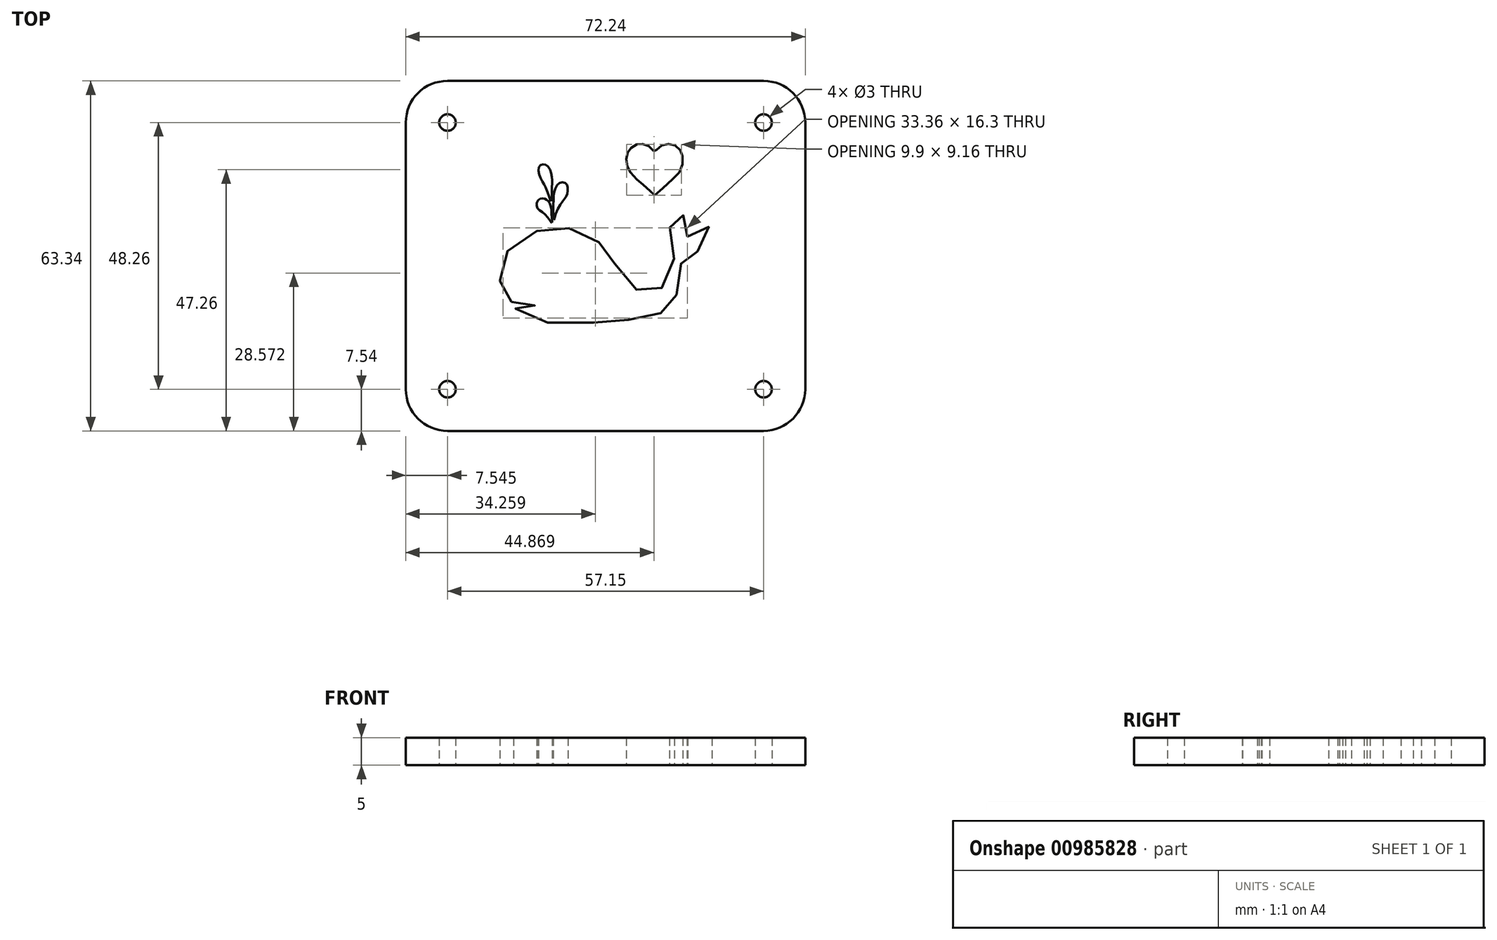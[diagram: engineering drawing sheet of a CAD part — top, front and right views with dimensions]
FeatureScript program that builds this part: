
annotation { "Feature Type Name" : "Feature", "Feature Type Description" : "" }
export const myFeature = defineFeature(function(context is Context, id is Id, definition is map)
    precondition{}
    {
        {
            var Q0;
            Q0=qCreatedBy(makeId("Top.planeOp"),FACE);
            var sketch = newSketch(context, id + "F0", { "sketchPlane" : qUnion([Q0])});
            skLineSegment(sketch, "E0.bottom", {"start": v(28.57, 31.67) * mm, "end": v(-28.58, 31.67) * mm});
            skLineSegment(sketch, "E0.top", {"start": v(28.58, -31.67) * mm, "end": v(-28.57, -31.67) * mm});
            skLineSegment(sketch, "E0.left", {"start": v(36.12, 24.13) * mm, "end": v(36.12, -24.13) * mm});
            skLineSegment(sketch, "E0.right", {"start": v(-36.12, 24.13) * mm, "end": v(-36.12, -24.13) * mm});
            skPoint(sketch, "E0.middle", {"position": v(0, 0) * mm});
            skPoint(sketch, "E1.visualSharp", {"position": v(-36.12, 31.67) * mm});
            skArc(sketch, "E1.filletArc", {"start": v(-28.58, 31.67) * mm, "mid": v(-33.9, 29.46) * mm, "end": v(-36.12, 24.13) * mm});
            skPoint(sketch, "E2.visualSharp", {"position": v(36.12, 31.67) * mm});
            skArc(sketch, "E2.filletArc", {"start": v(36.11, 24.13) * mm, "mid": v(33.9, 29.46) * mm, "end": v(28.57, 31.67) * mm});
            skPoint(sketch, "E3.visualSharp", {"position": v(36.12, -31.67) * mm});
            skArc(sketch, "E3.filletArc", {"start": v(28.58, -31.67) * mm, "mid": v(33.9, -29.46) * mm, "end": v(36.12, -24.13) * mm});
            skPoint(sketch, "E4.visualSharp", {"position": v(-36.11, -31.67) * mm});
            skArc(sketch, "E4.filletArc", {"start": v(-36.12, -24.13) * mm, "mid": v(-33.9, -29.46) * mm, "end": v(-28.57, -31.67) * mm});
            skCircle(sketch, "E5", {"center": v(-28.58, 24.13) * mm, "radius": 1.5 * mm});
            skCircle(sketch, "E6", {"center": v(28.57, 24.13) * mm, "radius": 1.5 * mm});
            skCircle(sketch, "E7", {"center": v(-28.57, -24.13) * mm, "radius": 1.5 * mm});
            skCircle(sketch, "E8", {"center": v(28.58, -24.13) * mm, "radius": 1.5 * mm});
            skFitSpline(sketch, "E9", {"points": [v(14.82, 3.5) * mm, v(16.2, 4.84) * mm, v(17.58, 5.43) * mm, v(18.71, 5.22) * mm, v(19.23, 4.15) * mm, v(18.37, 2.12) * mm, v(15.03, 0) * mm, v(14.37, -0.26) * mm, v(13.96, -0.4) * mm, v(13.7, -1.17) * mm, v(13.52, -1.93) * mm, v(13.25, -4.1) * mm, v(12.65, -7.62) * mm, v(12.02, -8.8) * mm, v(11.27, -9.7) * mm, v(9.38, -10.56) * mm, v(7.28, -10.99) * mm, v(3.97, -11.58) * mm, v(0.94, -12.03) * mm, v(-1.92, -12.1) * mm, v(-8.24, -12.13) * mm, v(-11.23, -11.95) * mm, v(-14.16, -11.03) * mm, v(-16.53, -9.26) * mm, v(-16.59, -9.08) * mm, v(-15.94, -9.26) * mm, v(-13.77, -9.26) * mm, v(-12.3, -8.65) * mm, v(-14.9, -8.73) * mm, v(-17.25, -8.1) * mm, v(-18.51, -6.13) * mm, v(-18.75, -5.54) * mm, v(-19.05, -4.75) * mm, v(-19.05, -2.52) * mm, v(-18.51, -0.38) * mm, v(-16.45, 2.24) * mm, v(-14.07, 3.88) * mm, v(-10.74, 4.94) * mm, v(-8.18, 5.16) * mm, v(-5.93, 4.9) * mm, v(-2.9, 3.72) * mm, v(-1.13, 2.44) * mm, v(0, 1.26) * mm, v(0.92, 0) * mm, v(2.2, -2.25) * mm, v(4.56, -5.28) * mm, v(5.62, -6.17) * mm, v(6.86, -6.84) * mm, v(8.71, -7.07) * mm, v(11, -4.6) * mm, v(11.51, -3.31) * mm, v(12.42, -0.32) * mm, v(12.12, 1.97) * mm, v(11.59, 4.74) * mm, v(11.79, 6.08) * mm, v(12.3, 7.08) * mm, v(13.36, 7.6) * mm, v(14.5, 6.93) * mm, v(14.88, 5.47) * mm, v(14.76, 3.91) * mm, v(14.82, 3.5) * mm]});
            skFitSpline(sketch, "E10", {"points": [v(-9.68, 6) * mm, v(-9.75, 7.66) * mm, v(-9.91, 9.05) * mm, v(-10.43, 9.96) * mm, v(-11.1, 10.4) * mm, v(-12.11, 10.14) * mm, v(-12.4, 8.85) * mm, v(-11.12, 7.66) * mm, v(-9.83, 6.13) * mm, v(-9.68, 6) * mm]});
            skFitSpline(sketch, "E11", {"points": [v(-9.83, 9.9) * mm, v(-9.68, 12.74) * mm, v(-9.68, 14.15) * mm, v(-10.23, 15.95) * mm, v(-11.15, 16.56) * mm, v(-11.93, 16.27) * mm, v(-11.98, 14.74) * mm, v(-11.22, 13.09) * mm, v(-10.5, 11.65) * mm, v(-9.83, 9.9) * mm]});
            skFitSpline(sketch, "E12", {"points": [v(-9.37, 6.55) * mm, v(-8.75, 8.22) * mm, v(-7.4, 10.32) * mm, v(-6.98, 11.07) * mm, v(-6.83, 12.46) * mm, v(-7.31, 13.2) * mm, v(-8.3, 13.22) * mm, v(-9.15, 11.93) * mm, v(-9.43, 9.9) * mm, v(-9.37, 6.55) * mm]});
            skFitSpline(sketch, "E13", {"points": [v(8.92, 11) * mm, v(11.2, 13.12) * mm, v(13.12, 14.88) * mm, v(13.83, 16.27) * mm, v(13.95, 17.88) * mm, v(13.75, 18.7) * mm, v(13.14, 19.58) * mm, v(12.1, 20.2) * mm, v(11.02, 20.25) * mm, v(10.1, 19.98) * mm, v(9.2, 19.22) * mm, v(8.88, 18.77) * mm, v(8.69, 19.09) * mm, v(7.86, 19.83) * mm, v(6.86, 20.2) * mm, v(6.2, 20.25) * mm, v(5.42, 20.08) * mm, v(4.6, 19.5) * mm, v(4.12, 18.9) * mm, v(3.82, 18.13) * mm, v(3.84, 16.82) * mm, v(4.1, 15.83) * mm, v(4.71, 14.85) * mm, v(6.17, 13.4) * mm, v(7.3, 12.46) * mm, v(8.65, 11.16) * mm, v(8.92, 11) * mm]});
            skSolve(sketch);
        }
        {
            var Q0;
            Q0=qSketchRegion(id+"F0",true);
            extrude(context, id + "F1", {"entities" : qUnion([Q0]), "depth" : 5 * mm, "offsetDistance" : 25 * mm});
        }
    });
